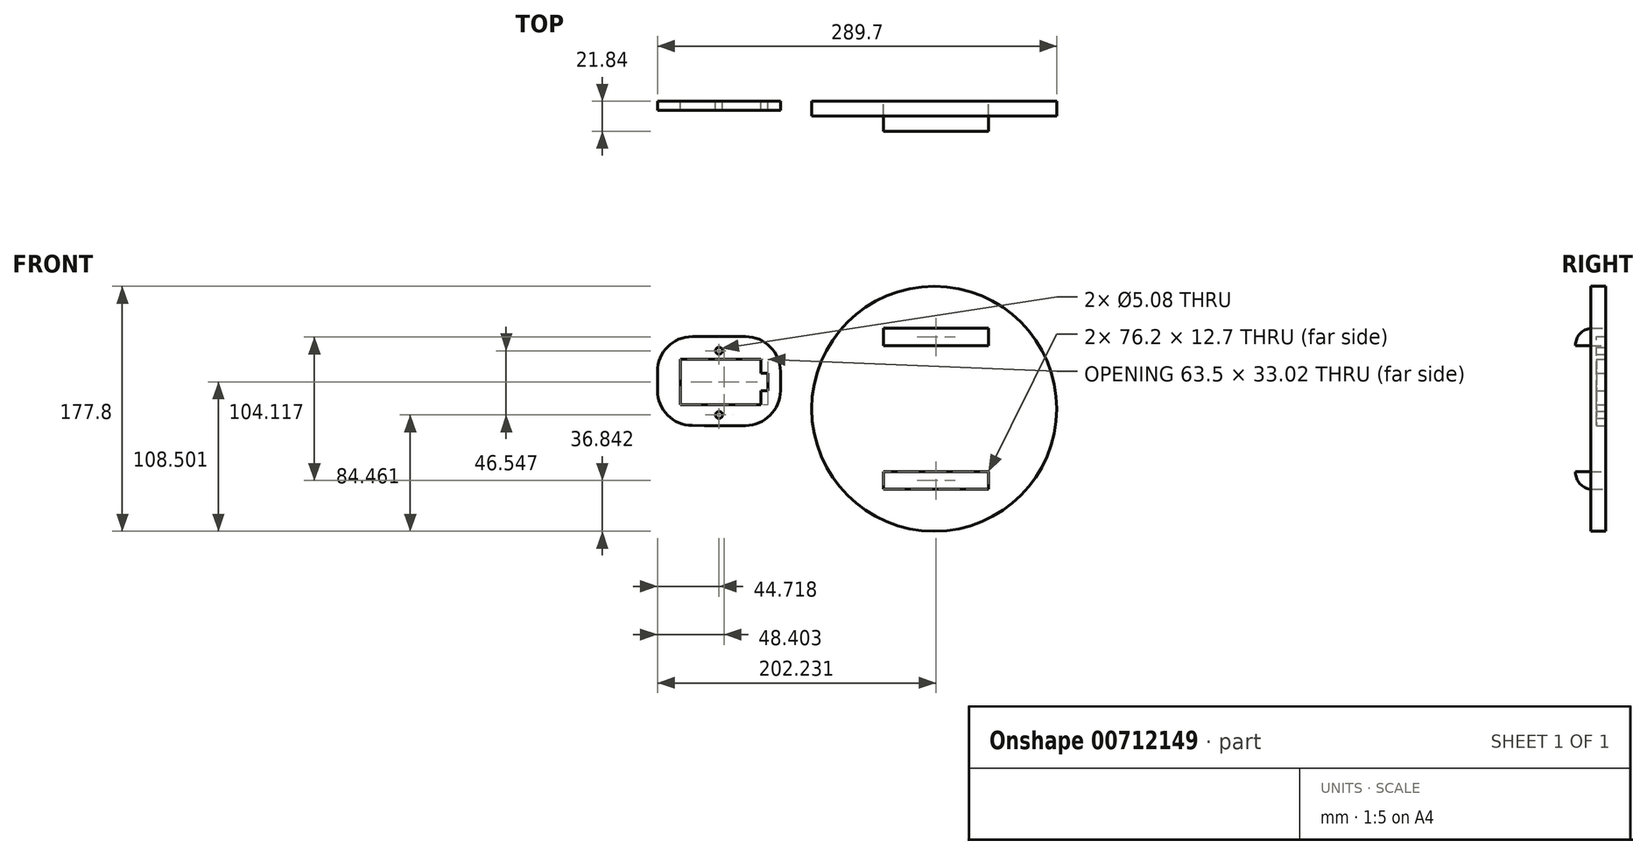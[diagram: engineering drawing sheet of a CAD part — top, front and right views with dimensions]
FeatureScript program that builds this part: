
annotation { "Feature Type Name" : "Feature", "Feature Type Description" : "" }
export const myFeature = defineFeature(function(context is Context, id is Id, definition is map)
    precondition{}
    {
        {
            var Q0;
            Q0=qCreatedBy(makeId("Front.planeOp"),FACE);
            var sketch = newSketch(context, id + "F0", { "sketchPlane" : qUnion([Q0])});
            skLineSegment(sketch, "E0", {"start": v(-49.96, 36.11) * mm, "end": v(-49.96, 3.1) * mm});
            skLineSegment(sketch, "E1", {"start": v(-49.96, 3.1) * mm, "end": v(8.46, 3.1) * mm});
            skLineSegment(sketch, "E2", {"start": v(8.46, 3.1) * mm, "end": v(8.46, 13.25) * mm});
            skLineSegment(sketch, "E3", {"start": v(8.46, 13.25) * mm, "end": v(13.54, 13.25) * mm});
            skLineSegment(sketch, "E4", {"start": v(13.54, 13.25) * mm, "end": v(13.54, 25.95) * mm});
            skLineSegment(sketch, "E5", {"start": v(13.54, 25.95) * mm, "end": v(8.46, 25.95) * mm});
            skLineSegment(sketch, "E6", {"start": v(8.46, 25.95) * mm, "end": v(8.46, 36.11) * mm});
            skLineSegment(sketch, "E7", {"start": v(8.46, 36.11) * mm, "end": v(-49.96, 36.11) * mm});
            skCircle(sketch, "E8", {"center": v(-21.9, 42.1) * mm, "radius": 2.54 * mm});
            skCircle(sketch, "E9", {"center": v(-21.9, -4.44) * mm, "radius": 2.54 * mm});
            skLineSegment(sketch, "E10", {"start": v(-32.36, -12.15) * mm, "end": v(22.6, -12.15) * mm});
            skLineSegment(sketch, "E11", {"start": v(22.6, -12.15) * mm, "end": v(22.6, 52.42) * mm});
            skLineSegment(sketch, "E12", {"start": v(22.6, 52.42) * mm, "end": v(-66.61, 52.42) * mm});
            skLineSegment(sketch, "E13", {"start": v(-66.61, 52.42) * mm, "end": v(-66.61, -12.05) * mm});
            skLineSegment(sketch, "E14", {"start": v(-66.61, -12.05) * mm, "end": v(-32.36, -12.15) * mm});
            skSolve(sketch);
        }
        {
            var Q0;
            Q0=makeQuery(id+"F0.imprint","IMPRINT",FACE,{"disambiguationData":[TD([[makeQuery(id+"F0.imprint","IMPRINT",EDGE,{"derivedFrom":sQuery(id+"F0.wireOp",EDGE,"E0")}),-1.0]])]});
            extrude(context, id + "F1", {"entities" : qUnion([Q0]), "depth" : 6.6 * mm, "offsetDistance" : 25.4 * mm});
        }
        {
            var Q0;
            Q0=makeQuery(id+"F1.opExtrude","SWEPT_EDGE",EDGE,{"disambiguationData":[OSD([sQuery(id+"F0.wireOp",EDGE,"E10"),sQuery(id+"F0.wireOp",EDGE,"E11")])]});
            fillet(context, id + "F2", {"entities" : qUnion([Q0]), "radius" : 25.4 * mm, "tangentPropagation" : true, "allowEdgeOverflow" : false});
        }
        {
            var Q0;
            Q0=makeQuery(id+"F1.opExtrude","SWEPT_EDGE",EDGE,{"disambiguationData":[OSD([sQuery(id+"F0.wireOp",EDGE,"E11"),sQuery(id+"F0.wireOp",EDGE,"E12")])]});
            fillet(context, id + "F3", {"entities" : qUnion([Q0]), "radius" : 25.4 * mm, "tangentPropagation" : true, "allowEdgeOverflow" : false});
        }
        {
            var Q0;
            Q0=makeQuery(id+"F1.opExtrude","SWEPT_EDGE",EDGE,{"disambiguationData":[OSD([sQuery(id+"F0.wireOp",EDGE,"E12"),sQuery(id+"F0.wireOp",EDGE,"E13")])]});
            fillet(context, id + "F4", {"entities" : qUnion([Q0]), "radius" : 25.4 * mm, "tangentPropagation" : true, "allowEdgeOverflow" : false});
        }
        {
            var Q0;
            Q0=makeQuery(id+"F1.opExtrude","SWEPT_EDGE",EDGE,{"disambiguationData":[OSD([sQuery(id+"F0.wireOp",EDGE,"E13"),sQuery(id+"F0.wireOp",EDGE,"E14")])]});
            fillet(context, id + "F5", {"entities" : qUnion([Q0]), "radius" : 25.4 * mm, "tangentPropagation" : true, "allowEdgeOverflow" : false});
        }
        {
            var Q0;
            Q0=qCreatedBy(makeId("Front.planeOp"),FACE);
            var sketch = newSketch(context, id + "F6", { "sketchPlane" : qUnion([Q0])});
            skCircle(sketch, "E15", {"center": v(134.2, 0) * mm, "radius": 88.9 * mm});
            skCircle(sketch, "E16", {"center": v(134.2, 0) * mm, "radius": 2.54 * mm});
            skLineSegment(sketch, "E17", {"start": v(135.62, 58.4) * mm, "end": v(173.72, 58.4) * mm});
            skLineSegment(sketch, "E18", {"start": v(173.72, 58.4) * mm, "end": v(97.52, 58.4) * mm});
            skLineSegment(sketch, "E19", {"start": v(97.52, 58.4) * mm, "end": v(97.52, 45.7) * mm});
            skLineSegment(sketch, "E20", {"start": v(97.52, 45.7) * mm, "end": v(173.72, 45.7) * mm});
            skLineSegment(sketch, "E21", {"start": v(173.72, 45.7) * mm, "end": v(173.72, 58.4) * mm});
            skLineSegment(sketch, "E22", {"start": v(135.62, -58.4) * mm, "end": v(97.52, -58.4) * mm});
            skLineSegment(sketch, "E23", {"start": v(97.52, -58.4) * mm, "end": v(173.72, -58.4) * mm});
            skLineSegment(sketch, "E24", {"start": v(173.72, -58.4) * mm, "end": v(173.72, -45.7) * mm});
            skLineSegment(sketch, "E25", {"start": v(173.72, -45.7) * mm, "end": v(97.52, -45.7) * mm});
            skLineSegment(sketch, "E26", {"start": v(97.52, -45.7) * mm, "end": v(97.52, -58.4) * mm});
            skSolve(sketch);
        }
        {
            var Q0;
            {var subQ0=sQuery(id+"F6.wireOp",EDGE,"E19");Q0=makeQuery(id+"F6.imprint","IMPRINT",FACE,{"disambiguationData":[TD([[makeQuery(id+"F6.imprint","IMPRINT",EDGE,{"derivedFrom":subQ0}),1.0]])]});}
            var Q1;
            {var subQ0=sQuery(id+"F6.wireOp",EDGE,"E24");Q1=makeQuery(id+"F6.imprint","IMPRINT",FACE,{"disambiguationData":[TD([[makeQuery(id+"F6.imprint","IMPRINT",EDGE,{"derivedFrom":subQ0}),1.0]])]});}
            extrude(context, id + "F7", {"entities" : qUnion([Q0, Q1]), "depth" : 21.84 * mm, "offsetDistance" : 25.4 * mm});
        }
        {
            var Q0;
            Q0 = qSketchRegion(id + "F6", true);
            extrude(context, id + "F8", {"entities" : qUnion([Q0]), "depth" : 10.67 * mm, "offsetDistance" : 25.4 * mm});
        }
        {
            var Q0;
            Q0=makeQuery(id+"F7.opExtrude","CAP_EDGE",EDGE,{"disambiguationData":[OSD([sQuery(id+"F6.wireOp",EDGE,"E23")])],"isStart":false});
            fillet(context, id + "F9", {"entities" : qUnion([Q0]), "radius" : 12.26 * mm, "tangentPropagation" : true, "allowEdgeOverflow" : false});
        }
        {
            var Q0;
            Q0=makeQuery(id+"F7.opExtrude","CAP_EDGE",EDGE,{"disambiguationData":[OSD([sQuery(id+"F6.wireOp",EDGE,"E18")])],"isStart":false});
            fillet(context, id + "F10", {"entities" : qUnion([Q0]), "radius" : 12.26 * mm, "tangentPropagation" : true, "allowEdgeOverflow" : false});
        }
        {
            var Q0;
            Q0=qCreatedBy(makeId("Front.planeOp"),FACE);
            var sketch = newSketch(context, id + "F11", { "sketchPlane" : qUnion([Q0])});
            skCircle(sketch, "E27", {"center": v(134.2, 0) * mm, "radius": 8.9 * mm});
            skSolve(sketch);
        }
        {
            var Q0;
            Q0=sQuery(id+"F11.wireOp",VERTEX,"E27.center");
            var Q1;
            Q1=makeQuery(id+"F8.opExtrude","SWEPT_BODY",BODY,{"disambiguationData":[OSD([sQuery(id+"F6.wireOp",EDGE,"E15"),sQuery(id+"F6.wireOp",EDGE,"E16"),sQuery(id+"F6.wireOp",EDGE,"E18"),sQuery(id+"F6.wireOp",EDGE,"E19"),sQuery(id+"F6.wireOp",EDGE,"E20"),sQuery(id+"F6.wireOp",EDGE,"E21"),sQuery(id+"F6.wireOp",EDGE,"E23"),sQuery(id+"F6.wireOp",EDGE,"E24"),sQuery(id+"F6.wireOp",EDGE,"E25"),sQuery(id+"F6.wireOp",EDGE,"E26")])]});
            hole(context, id + "F12", {"style" : HoleStyle.SIMPLE, "endStyle" : HoleEndStyle.THROUGH, "oppositeDirection" : true, "holeDiameter" : 17.78 * mm, "majorDiameter" : 6.35 * mm, "isTappedThrough" : true, "tappedDepth" : 12.7 * mm, "tapClearance" : 3, "locations" : qUnion([Q0]), "scope" : qUnion([Q1])});
        }
        {
            var Q0;
            Q0 = qSketchRegion(id + "F11", true);
            extrude(context, id + "F13", {"entities" : qUnion([Q0]), "operationType" : NewBodyOperationType.ADD, "depth" : 7.62 * mm, "offsetDistance" : 25.4 * mm});
        }
        {
            var Q0;
            Q0=makeQuery(id+"F13.opExtrude","CAP_FACE",FACE,{"disambiguationData":[OSD([sQuery(id+"F11.wireOp",EDGE,"E27")])],"isStart":false});
            extrude(context, id + "F14", {"entities" : qUnion([Q0]), "operationType" : NewBodyOperationType.ADD, "depth" : 3.05 * mm, "offsetDistance" : 25.4 * mm});
        }
        {
            var Q0;
            Q0=qCreatedBy(makeId("Front.planeOp"),FACE);
            var sketch = newSketch(context, id + "F15", { "sketchPlane" : qUnion([Q0])});
            skCircle(sketch, "E28", {"center": v(132.7, 0) * mm, "radius": 8.9 * mm});
            skSolve(sketch);
        }
        {
            var Q0;
            Q0=makeQuery(id+"F15.imprint","IMPRINT",FACE,{"disambiguationData":[TD([[makeQuery(id+"F15.imprint","IMPRINT",EDGE,{"derivedFrom":sQuery(id+"F15.wireOp",EDGE,"E28")}),1.0]])]});
            extrude(context, id + "F16", {"entities" : qUnion([Q0]), "operationType" : NewBodyOperationType.ADD, "depth" : 2.03 * mm, "offsetDistance" : 25.4 * mm});
        }
        {
            var Q0;
            Q0 = qSketchRegion(id + "F15", true);
            extrude(context, id + "F17", {"entities" : qUnion([Q0]), "operationType" : NewBodyOperationType.ADD, "depth" : 2.3 * mm, "offsetDistance" : 25.4 * mm});
        }
        {
            var Q0;
            Q0=qCreatedBy(makeId("Front.planeOp"),FACE);
            var sketch = newSketch(context, id + "F18", { "sketchPlane" : qUnion([Q0])});
            skCircle(sketch, "E29", {"center": v(135.06, 0) * mm, "radius": 8.9 * mm});
            skSolve(sketch);
        }
        {
            var Q0;
            Q0 = qSketchRegion(id + "F18", true);
            extrude(context, id + "F19", {"entities" : qUnion([Q0]), "operationType" : NewBodyOperationType.ADD, "depth" : 5.33 * mm, "offsetDistance" : 25.4 * mm});
        }
        {
            var Q0;
            Q0=makeQuery(id+"F1.opExtrude","SWEPT_FACE",FACE,{"disambiguationData":[OSD([sQuery(id+"F0.wireOp",EDGE,"E0")])]});
            extrude(context, id + "F20", {"entities" : qUnion([Q0]), "operationType" : NewBodyOperationType.ADD, "oppositeDirection" : true, "depth" : 5.08 * mm, "offsetDistance" : 25.4 * mm});
        }
    });
